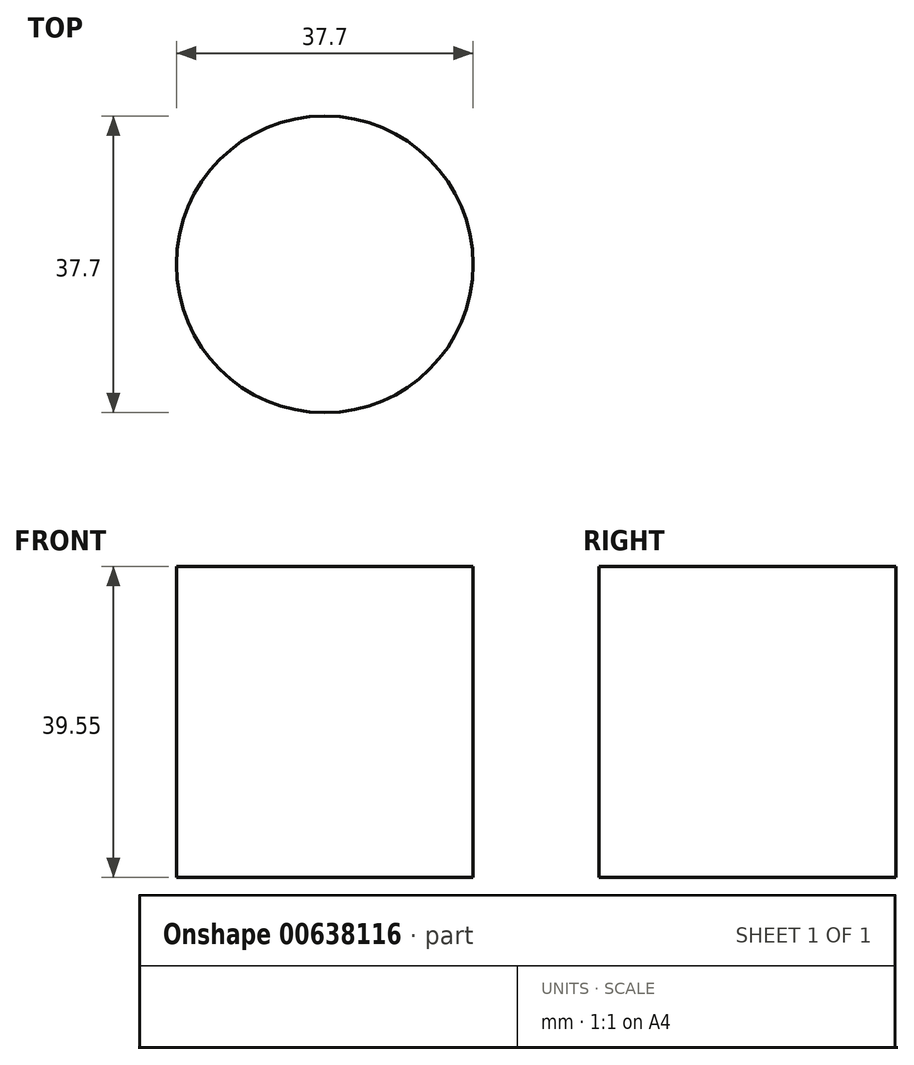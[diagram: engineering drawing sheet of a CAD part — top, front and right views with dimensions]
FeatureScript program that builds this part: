
annotation { "Feature Type Name" : "Feature", "Feature Type Description" : "" }
export const myFeature = defineFeature(function(context is Context, id is Id, definition is map)
    precondition{}
    {
        {
            var Q0;
            Q0=qCreatedBy(makeId("Top.planeOp"),FACE);
            var sketch = newSketch(context, id + "F0", { "sketchPlane" : qUnion([Q0])});
            skCircle(sketch, "E0", {"center": v(0, 0) * mm, "radius": 18.85 * mm});
            skSolve(sketch);
        }
        {
            var Q0;
            Q0 = qSketchRegion(id + "F0", true);
            extrude(context, id + "F1", {"entities" : qUnion([Q0]), "depth" : 39.55 * mm, "offsetDistance" : 25 * mm});
        }
    });
